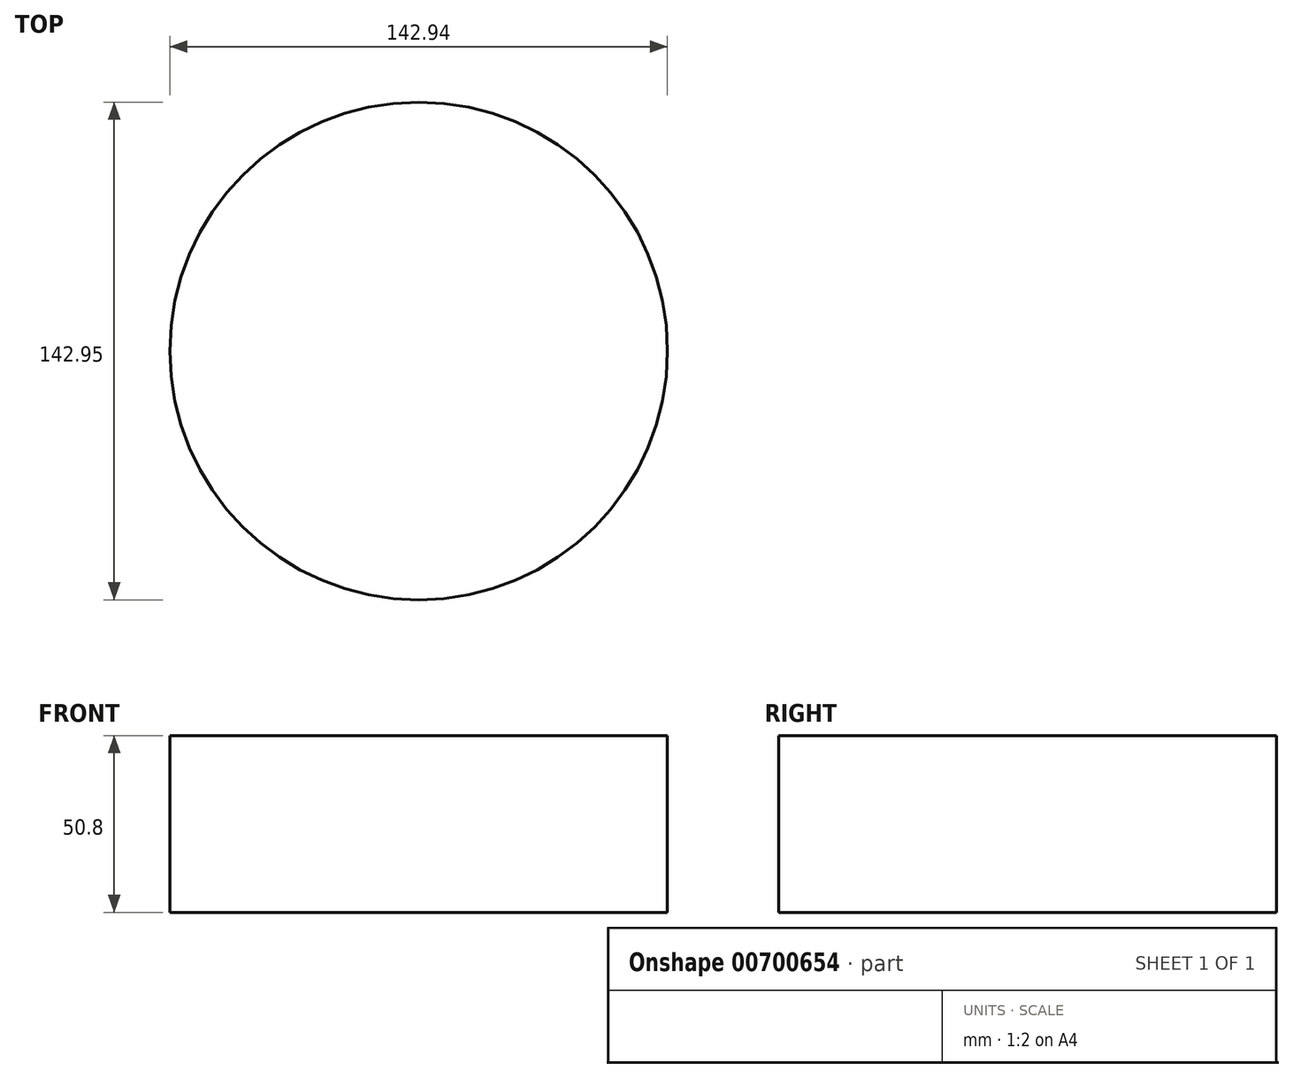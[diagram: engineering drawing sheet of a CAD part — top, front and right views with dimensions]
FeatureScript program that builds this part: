
annotation { "Feature Type Name" : "Feature", "Feature Type Description" : "" }
export const myFeature = defineFeature(function(context is Context, id is Id, definition is map)
    precondition{}
    {
        {
            var Q0;
            Q0=qCreatedBy(makeId("Top.planeOp"),FACE);
            var sketch = newSketch(context, id + "F0", { "sketchPlane" : qUnion([Q0])});
            skCircle(sketch, "E0", {"center": v(0, 10.64) * mm, "radius": 71.47 * mm});
            skSolve(sketch);
        }
        {
            var Q0;
            Q0=makeQuery(id+"F0.imprint","IMPRINT",FACE,{"disambiguationData":[TD([[makeQuery(id+"F0.imprint","IMPRINT",EDGE,{"derivedFrom":sQuery(id+"F0.wireOp",EDGE,"E0")}),1.0]])]});
            extrude(context, id + "F1", {"entities" : qUnion([Q0]), "depth" : 50.8 * mm, "offsetDistance" : 25.4 * mm});
        }
    });
